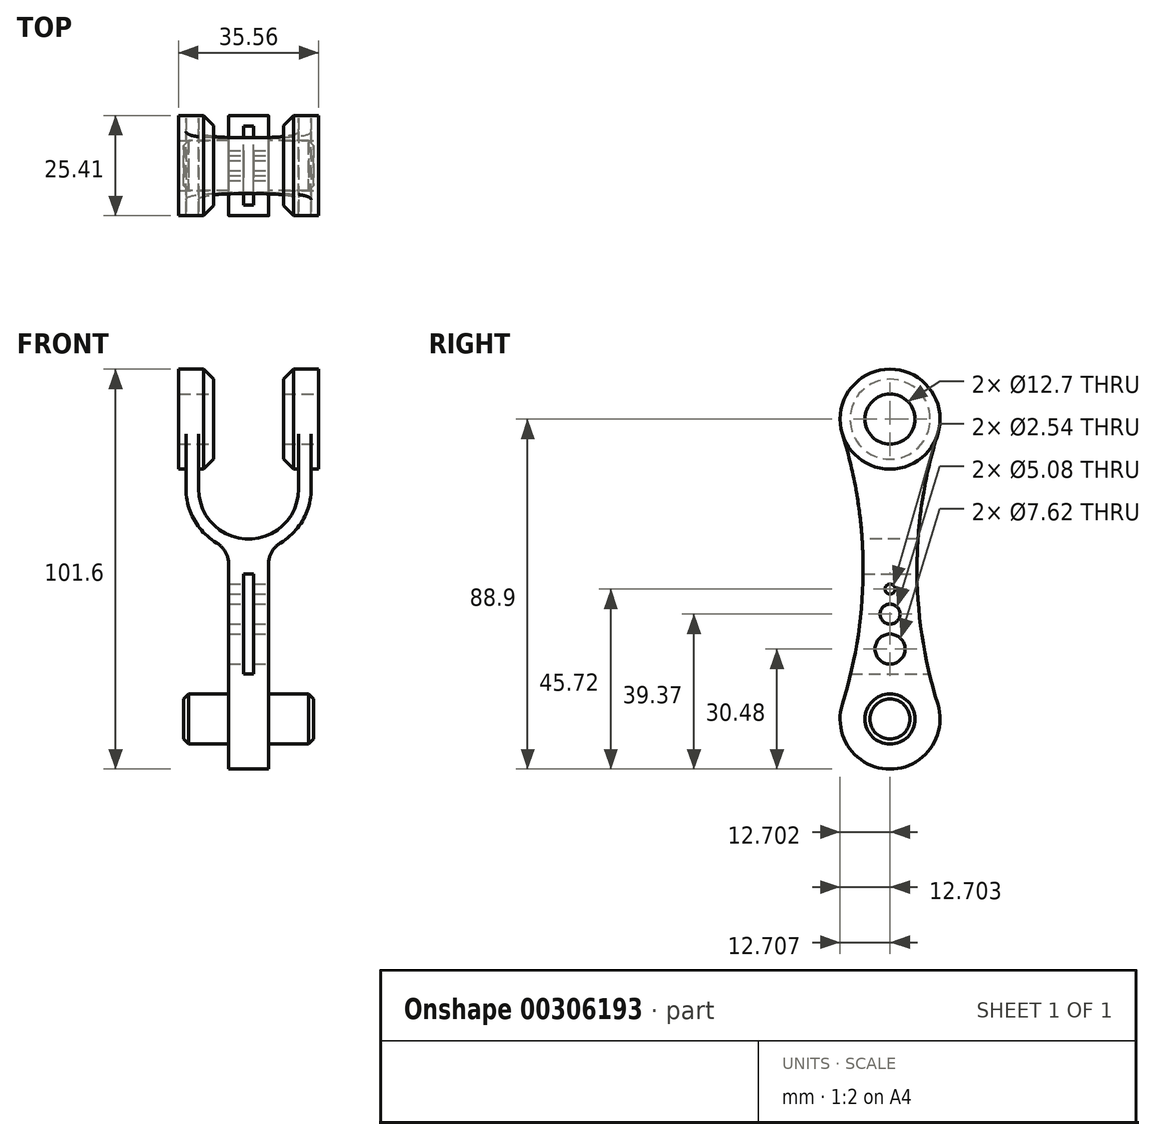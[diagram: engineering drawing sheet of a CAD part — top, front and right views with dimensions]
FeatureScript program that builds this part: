
annotation { "Feature Type Name" : "Feature", "Feature Type Description" : "" }
export const myFeature = defineFeature(function(context is Context, id is Id, definition is map)
    precondition{}
    {
        {
            var Q0;
            Q0=qCreatedBy(makeId("Front.planeOp"),FACE);
            var sketch = newSketch(context, id + "F0", { "sketchPlane" : qUnion([Q0])});
            skPoint(sketch, "E0.middle", {"position": v(0, 0) * mm});
            skArc(sketch, "E1", {"start": v(-8.17, -19.4) * mm, "mid": v(-13.82, -25.2) * mm, "end": v(-15.88, -33.02) * mm});
            skLineSegment(sketch, "E2.bottom", {"start": v(-5.08, 2.35) * mm, "end": v(5.08, 2.35) * mm});
            skLineSegment(sketch, "E2.left", {"start": v(-5.08, 2.35) * mm, "end": v(-5.08, -13.95) * mm});
            skLineSegment(sketch, "E2.right", {"start": v(5.08, 2.35) * mm, "end": v(5.08, -13.95) * mm});
            skArc(sketch, "E3", {"start": v(12.7, -33.02) * mm, "mid": v(0, -20.32) * mm, "end": v(-12.7, -33.02) * mm});
            skLineSegment(sketch, "E4.top", {"start": v(14.22, -50.8) * mm, "end": v(14.36, -50.8) * mm});
            skLineSegment(sketch, "E4.left", {"start": v(12.7, -33.02) * mm, "end": v(12.7, -49.28) * mm});
            skLineSegment(sketch, "E4.right", {"start": v(15.88, -33.02) * mm, "end": v(15.88, -49.28) * mm});
            skLineSegment(sketch, "E5.top", {"start": v(-14.36, -50.8) * mm, "end": v(-14.22, -50.8) * mm});
            skLineSegment(sketch, "E5.left", {"start": v(-15.88, -33.02) * mm, "end": v(-15.88, -49.28) * mm});
            skLineSegment(sketch, "E5.right", {"start": v(-12.7, -33.02) * mm, "end": v(-12.7, -49.28) * mm});
            skArc(sketch, "E6.trimOffspring", {"start": v(15.88, -33.02) * mm, "mid": v(13.82, -25.2) * mm, "end": v(8.17, -19.4) * mm});
            skPoint(sketch, "E7.visualSharp", {"position": v(-5.08, -17.97) * mm});
            skArc(sketch, "E7.filletArc", {"start": v(-8.17, -19.4) * mm, "mid": v(-5.9, -17.08) * mm, "end": v(-5.08, -13.95) * mm});
            skPoint(sketch, "E8.visualSharp", {"position": v(5.08, -17.97) * mm});
            skArc(sketch, "E8.filletArc", {"start": v(5.08, -13.95) * mm, "mid": v(5.9, -17.08) * mm, "end": v(8.17, -19.4) * mm});
            skArc(sketch, "E9.filletArc", {"start": v(12.7, -49.28) * mm, "mid": v(13.15, -50.35) * mm, "end": v(14.22, -50.8) * mm});
            skArc(sketch, "E10.filletArc", {"start": v(14.36, -50.8) * mm, "mid": v(15.44, -50.35) * mm, "end": v(15.88, -49.28) * mm});
            skArc(sketch, "E11.filletArc", {"start": v(-15.88, -49.28) * mm, "mid": v(-15.44, -50.35) * mm, "end": v(-14.36, -50.8) * mm});
            skArc(sketch, "E12.filletArc", {"start": v(-14.22, -50.8) * mm, "mid": v(-13.15, -50.35) * mm, "end": v(-12.7, -49.28) * mm});
            skSolve(sketch);
        }
        {
            var Q0;
            Q0=qSketchRegion(id+"F0",true);
            extrude(context, id + "F1", {"entities" : qUnion([Q0]), "depth" : 38.1 * mm, "symmetric" : true});
        }
        {
            var Q0;
            Q0=qCreatedBy(makeId("Right.planeOp"),FACE);
            var sketch = newSketch(context, id + "F2", { "sketchPlane" : qUnion([Q0])});
            skCircle(sketch, "E13", {"center": v(0, -50.8) * mm, "radius": 6.35 * mm});
            skSolve(sketch);
        }
        {
            var Q0;
            Q0=qCreatedBy(makeId("Right.planeOp"),FACE);
            var sketch = newSketch(context, id + "F3", { "sketchPlane" : qUnion([Q0])});
            skCircle(sketch, "E14", {"center": v(0, -50.8) * mm, "radius": 12.7 * mm});
            skSolve(sketch);
        }
        {
            var Q0;
            Q0=qSketchRegion(id+"F3",true);
            extrude(context, id + "F4", {"entities" : qUnion([Q0]), "operationType" : NewBodyOperationType.ADD, "depth" : 35.56 * mm, "symmetric" : true});
        }
        {
            var Q0;
            Q0=qCreatedBy(makeId("Front.planeOp"),FACE);
            var sketch = newSketch(context, id + "F5", { "sketchPlane" : qUnion([Q0])});
            skLineSegment(sketch, "E15.bottom", {"start": v(8.9, -69.85) * mm, "end": v(-8.89, -69.85) * mm});
            skLineSegment(sketch, "E15.top", {"start": v(8.9, -31.75) * mm, "end": v(-8.89, -31.75) * mm});
            skLineSegment(sketch, "E15.left", {"start": v(8.9, -69.85) * mm, "end": v(8.9, -31.75) * mm});
            skLineSegment(sketch, "E15.right", {"start": v(-8.89, -69.85) * mm, "end": v(-8.89, -31.75) * mm});
            skPoint(sketch, "E15.middle", {"position": v(0, -50.8) * mm});
            skSolve(sketch);
        }
        {
            var Q0;
            Q0=qSketchRegion(id+"F2",true);
            extrude(context, id + "F6", {"entities" : qUnion([Q0]), "operationType" : NewBodyOperationType.REMOVE, "oppositeDirection" : true, "depth" : 76.2 * mm, "symmetric" : true});
        }
        {
            var Q0;
            Q0=qSketchRegion(id+"F5",true);
            extrude(context, id + "F7", {"entities" : qUnion([Q0]), "operationType" : NewBodyOperationType.REMOVE, "oppositeDirection" : true, "depth" : 38.1 * mm, "symmetric" : true});
        }
        {
            var Q0;
            Q0=makeQuery(id+"F7.boolean.opBoolean","INTERSECT",EDGE,{"derivedFrom":[makeQuery(id+"F4.opExtrude","SWEPT_FACE",FACE,{"disambiguationData":[OSD([sQuery(id+"F3.wireOp",EDGE,"E14")])]}),makeQuery(id+"F7.opExtrude","SWEPT_FACE",FACE,{"disambiguationData":[OSD([sQuery(id+"F5.wireOp",EDGE,"E15.right")])]})]});
            var Q1;
            Q1=makeQuery(id+"F7.boolean.opBoolean","INTERSECT",EDGE,{"derivedFrom":[makeQuery(id+"F4.opExtrude","SWEPT_FACE",FACE,{"disambiguationData":[OSD([sQuery(id+"F3.wireOp",EDGE,"E14")])]}),makeQuery(id+"F7.opExtrude","SWEPT_FACE",FACE,{"disambiguationData":[OSD([sQuery(id+"F5.wireOp",EDGE,"E15.left")])]})]});
            chamfer(context, id + "F8", {"entities" : qUnion([Q0, Q1]), "width" : 2.54 * mm, "tangentPropagation" : true});
        }
        {
            var Q0;
            Q0=qCreatedBy(makeId("Right.planeOp"),FACE);
            var sketch = newSketch(context, id + "F9", { "sketchPlane" : qUnion([Q0])});
            skArc(sketch, "E16", {"start": v(19.05, 25.39) * mm, "mid": v(0, 44.45) * mm, "end": v(-19.05, 25.39) * mm});
            skLineSegment(sketch, "E17.top", {"start": v(-19.05, -0.01) * mm, "end": v(19.05, -0.01) * mm});
            skLineSegment(sketch, "E17.left", {"start": v(-19.05, 25.39) * mm, "end": v(-19.05, -0.01) * mm});
            skLineSegment(sketch, "E17.right", {"start": v(19.05, 25.39) * mm, "end": v(19.05, -0.01) * mm});
            skSolve(sketch);
        }
        {
            var Q0;
            Q0=qSketchRegion(id+"F9",true);
            extrude(context, id + "F10", {"entities" : qUnion([Q0]), "operationType" : NewBodyOperationType.ADD, "depth" : 10.16 * mm, "symmetric" : true});
        }
        {
            var Q0;
            Q0=qCreatedBy(makeId("Right.planeOp"),FACE);
            var sketch = newSketch(context, id + "F11", { "sketchPlane" : qUnion([Q0])});
            skCircle(sketch, "E18", {"center": v(0, 25.4) * mm, "radius": 6.35 * mm});
            skSolve(sketch);
        }
        {
            var Q0;
            Q0=qSketchRegion(id+"F11",true);
            extrude(context, id + "F12", {"entities" : qUnion([Q0]), "operationType" : NewBodyOperationType.ADD, "depth" : 33.02 * mm, "symmetric" : true});
        }
        {
            var Q0;
            Q0=makeQuery(id+"F12.opExtrude","CAP_EDGE",EDGE,{"disambiguationData":[OSD([sQuery(id+"F11.wireOp",EDGE,"E18")])],"isStart":true});
            var Q1;
            Q1=makeQuery(id+"F12.opExtrude","CAP_EDGE",EDGE,{"disambiguationData":[OSD([sQuery(id+"F11.wireOp",EDGE,"E18")])],"isStart":false});
            chamfer(context, id + "F13", {"entities" : qUnion([Q0, Q1]), "width" : 1.27 * mm, "tangentPropagation" : true});
        }
        {
            var Q0;
            Q0=qCreatedBy(makeId("Right.planeOp"),FACE);
            var sketch = newSketch(context, id + "F14", { "sketchPlane" : qUnion([Q0])});
            skArc(sketch, "E19", {"start": v(12.12, 21.6) * mm, "mid": v(0, 38.1) * mm, "end": v(-12.12, 21.6) * mm});
            skArc(sketch, "E20", {"start": v(-12.12, -47) * mm, "mid": v(0, -63.5) * mm, "end": v(12.12, -47) * mm});
            skArc(sketch, "E21", {"start": v(12.12, 21.6) * mm, "mid": v(6.85, -12.7) * mm, "end": v(12.12, -47) * mm});
            skPoint(sketch, "E22.center.orphan", {"position": v(45.72, -6.35) * mm});
            skPoint(sketch, "E23.center.orphan", {"position": v(-45.72, -6.35) * mm});
            skArc(sketch, "E24", {"start": v(-12.12, -47) * mm, "mid": v(-6.85, -12.7) * mm, "end": v(-12.12, 21.6) * mm});
            skSolve(sketch);
        }
        {
            var Q0;
            Q0=qSketchRegion(id+"F14",true);
            extrude(context, id + "F15", {"entities" : qUnion([Q0]), "operationType" : NewBodyOperationType.INTERSECT, "depth" : 76.2 * mm, "symmetric" : true});
        }
        {
            var Q0;
            Q0=qCreatedBy(makeId("Front.planeOp"),FACE);
            var sketch = newSketch(context, id + "F16", { "sketchPlane" : qUnion([Q0])});
            skLineSegment(sketch, "E25.bottom", {"start": v(-1.27, -11.4) * mm, "end": v(1.27, -11.4) * mm});
            skLineSegment(sketch, "E25.top", {"start": v(-1.27, 14) * mm, "end": v(1.27, 14) * mm});
            skLineSegment(sketch, "E25.left", {"start": v(-1.27, -11.4) * mm, "end": v(-1.27, 14) * mm});
            skLineSegment(sketch, "E25.right", {"start": v(1.27, -11.4) * mm, "end": v(1.27, 14) * mm});
            skSolve(sketch);
        }
        {
            var Q0;
            Q0=qSketchRegion(id+"F16",true);
            extrude(context, id + "F17", {"entities" : qUnion([Q0]), "operationType" : NewBodyOperationType.REMOVE, "oppositeDirection" : true, "depth" : 50.8 * mm, "symmetric" : true});
        }
        {
            var Q0;
            Q0=qCreatedBy(makeId("Right.planeOp"),FACE);
            var sketch = newSketch(context, id + "F18", { "sketchPlane" : qUnion([Q0])});
            skCircle(sketch, "E26", {"center": v(0, 7.62) * mm, "radius": 3.81 * mm});
            skCircle(sketch, "E27", {"center": v(0, -1.27) * mm, "radius": 2.54 * mm});
            skCircle(sketch, "E28", {"center": v(0, -7.62) * mm, "radius": 1.27 * mm});
            skSolve(sketch);
        }
        {
            var Q0;
            Q0=qSketchRegion(id+"F18",true);
            extrude(context, id + "F19", {"entities" : qUnion([Q0]), "operationType" : NewBodyOperationType.REMOVE, "oppositeDirection" : true, "depth" : 25.4 * mm, "symmetric" : true});
        }
        {
            var Q0;
            Q0=makeQuery(id+"F1.opExtrude","SWEPT_BODY",BODY,{"disambiguationData":[OSD([sQuery(id+"F0.wireOp",EDGE,"E1"),sQuery(id+"F0.wireOp",EDGE,"E2.bottom"),sQuery(id+"F0.wireOp",EDGE,"E2.left"),sQuery(id+"F0.wireOp",EDGE,"E2.right"),sQuery(id+"F0.wireOp",EDGE,"E3"),sQuery(id+"F0.wireOp",EDGE,"E4.top"),sQuery(id+"F0.wireOp",EDGE,"E4.left"),sQuery(id+"F0.wireOp",EDGE,"E4.right"),sQuery(id+"F0.wireOp",EDGE,"E5.top"),sQuery(id+"F0.wireOp",EDGE,"E5.left"),sQuery(id+"F0.wireOp",EDGE,"E5.right"),sQuery(id+"F0.wireOp",EDGE,"E6.trimOffspring"),sQuery(id+"F0.wireOp",EDGE,"E7.filletArc"),sQuery(id+"F0.wireOp",EDGE,"E8.filletArc"),sQuery(id+"F0.wireOp",EDGE,"E9.filletArc"),sQuery(id+"F0.wireOp",EDGE,"E10.filletArc"),sQuery(id+"F0.wireOp",EDGE,"E11.filletArc"),sQuery(id+"F0.wireOp",EDGE,"E12.filletArc")])]});
            var Q1;
            {var subQ0=sQuery(id+"F11.wireOp",EDGE,"E18");Q1=makeQuery(id+"F13.opChamfer","BLEND_EDGE",EDGE,{"blendedFrom":[makeQuery(id+"F12.opExtrude","CAP_EDGE",EDGE,{"disambiguationData":[OSD([subQ0])],"isStart":false}),makeQuery(id+"F12.boolean.opBoolean","SPLIT",FACE,{"disambiguationData":[TD([makeQuery(id+"F1.opExtrude","SWEPT_FACE",FACE,{"disambiguationData":[OSD([sQuery(id+"F0.wireOp",EDGE,"E2.right")])]})])],"derivedFrom":makeQuery(id+"F12.opExtrude","SWEPT_FACE",FACE,{"disambiguationData":[OSD([subQ0])]})})],"blendedInto":[makeQuery(id+"F12.boolean.opBoolean","SPLIT",FACE,{"disambiguationData":[TD([makeQuery(id+"F1.opExtrude","SWEPT_FACE",FACE,{"disambiguationData":[OSD([sQuery(id+"F0.wireOp",EDGE,"E2.right")])]})])],"derivedFrom":makeQuery(id+"F12.opExtrude","SWEPT_FACE",FACE,{"disambiguationData":[OSD([subQ0])]})})]});}
            transform(context, id + "F20", {"entities" : qUnion([Q0]), "transformType" : TransformType.ROTATION, "transformAxis" : qUnion([Q1]), "angle" : 3.14 * radian, "makeCopy" : false});
        }
        {
            var Q0;
            Q0=qCreatedBy(makeId("Front.planeOp"),FACE);
            var sketch = newSketch(context, id + "F21", { "sketchPlane" : qUnion([Q0])});
            skLineSegment(sketch, "E29", {"start": v(17.78, 101.6) * mm, "end": v(-17.78, 101.6) * mm, "construction": true});
            skLineSegment(sketch, "E30", {"start": v(0, 0) * mm, "end": v(0, 101.6) * mm, "construction": true});
            skSolve(sketch);
        }
        {
            var Q0;
            Q0=makeQuery(id+"F1.opExtrude","SWEPT_BODY",BODY,{"disambiguationData":[OSD([sQuery(id+"F0.wireOp",EDGE,"E1"),sQuery(id+"F0.wireOp",EDGE,"E2.bottom"),sQuery(id+"F0.wireOp",EDGE,"E2.left"),sQuery(id+"F0.wireOp",EDGE,"E2.right"),sQuery(id+"F0.wireOp",EDGE,"E3"),sQuery(id+"F0.wireOp",EDGE,"E4.top"),sQuery(id+"F0.wireOp",EDGE,"E4.left"),sQuery(id+"F0.wireOp",EDGE,"E4.right"),sQuery(id+"F0.wireOp",EDGE,"E5.top"),sQuery(id+"F0.wireOp",EDGE,"E5.left"),sQuery(id+"F0.wireOp",EDGE,"E5.right"),sQuery(id+"F0.wireOp",EDGE,"E6.trimOffspring"),sQuery(id+"F0.wireOp",EDGE,"E7.filletArc"),sQuery(id+"F0.wireOp",EDGE,"E8.filletArc"),sQuery(id+"F0.wireOp",EDGE,"E9.filletArc"),sQuery(id+"F0.wireOp",EDGE,"E10.filletArc"),sQuery(id+"F0.wireOp",EDGE,"E11.filletArc"),sQuery(id+"F0.wireOp",EDGE,"E12.filletArc")])]});
            var Q1;
            Q1=sQuery(id+"F21.wireOp",EDGE,"E30");
            transform(context, id + "F22", {"entities" : qUnion([Q0]), "transformType" : TransformType.TRANSLATION_ENTITY, "oppositeDirectionEntity" : true, "transformLine" : qUnion([Q1]), "makeCopy" : false});
        }
    });
